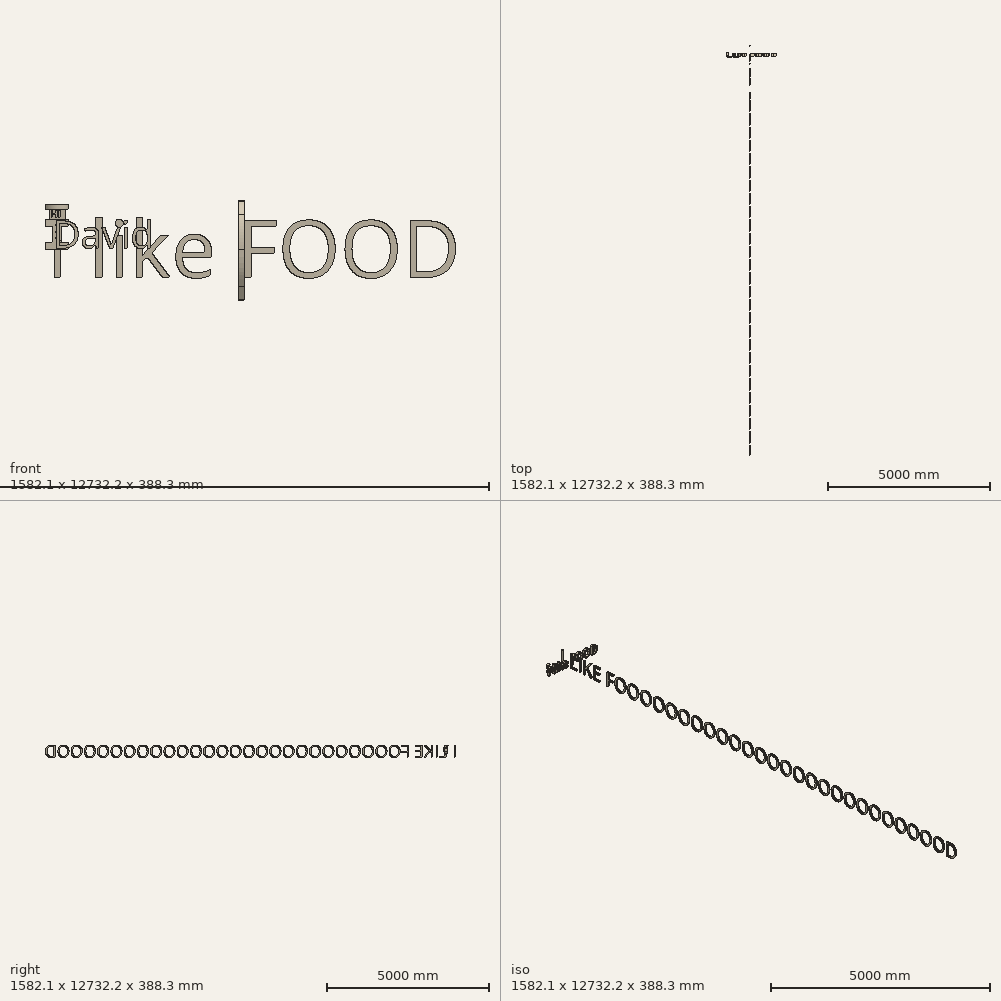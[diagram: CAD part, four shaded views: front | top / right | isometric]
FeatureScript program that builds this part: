
annotation { "Feature Type Name" : "Feature", "Feature Type Description" : "" }
export const myFeature = defineFeature(function(context is Context, id is Id, definition is map)
    precondition{}
    {
        {
            var Q0;
            Q0=qCreatedBy(makeId("Front.planeOp"),FACE);
            var sketch = newSketch(context, id + "F0", { "sketchPlane" : qUnion([Q0])});
            skLineSegment(sketch, "E0", {"start": v(-45.38, -52.7) * mm, "end": v(43.52, -52.7) * mm});
            skLineSegment(sketch, "E1", {"start": v(43.52, -52.7) * mm, "end": v(43.52, -27.3) * mm});
            skLineSegment(sketch, "E2", {"start": v(43.52, -27.3) * mm, "end": v(18.12, -27.3) * mm});
            skLineSegment(sketch, "E3", {"start": v(18.12, -27.3) * mm, "end": v(18.12, 36.2) * mm});
            skLineSegment(sketch, "E4", {"start": v(18.12, 36.2) * mm, "end": v(43.52, 36.2) * mm});
            skLineSegment(sketch, "E5", {"start": v(43.52, 36.2) * mm, "end": v(43.52, 61.6) * mm});
            skLineSegment(sketch, "E6", {"start": v(43.52, 61.6) * mm, "end": v(-45.38, 61.6) * mm});
            skLineSegment(sketch, "E7", {"start": v(-45.38, 61.6) * mm, "end": v(-45.38, 36.2) * mm});
            skLineSegment(sketch, "E8", {"start": v(-45.38, 36.2) * mm, "end": v(-19.98, 36.2) * mm});
            skLineSegment(sketch, "E9", {"start": v(-19.98, 36.2) * mm, "end": v(-19.98, -27.3) * mm});
            skLineSegment(sketch, "E10", {"start": v(-19.98, -27.3) * mm, "end": v(-45.38, -27.3) * mm});
            skLineSegment(sketch, "E11", {"start": v(-45.38, -27.3) * mm, "end": v(-45.38, -52.7) * mm});
            skSolve(sketch);
        }
        {
            var Q0;
            Q0=makeQuery(id+"F0.imprint","IMPRINT",FACE,{"disambiguationData":[TD([[makeQuery(id+"F0.imprint","IMPRINT",EDGE,{"derivedFrom":sQuery(id+"F0.wireOp",EDGE,"E0")}),1.0]])]});
            extrude(context, id + "F1", {"entities" : qUnion([Q0]), "depth" : 76.2 * mm});
        }
        {
            var Q0;
            Q0=makeQuery(id+"F1.opExtrude","SWEPT_FACE",FACE,{"disambiguationData":[OSD([sQuery(id+"F0.wireOp",EDGE,"E9")])]});
            var sketch = newSketch(context, id + "F2", { "sketchPlane" : qUnion([Q0])});
            skCircle(sketch, "E12", {"center": v(38.1, 4.44) * mm, "radius": 23.75 * mm});
            skPoint(sketch, "E12.centerSnap0", {"position": v(0, 4.44) * mm});
            skPoint(sketch, "E12.centerSnap1", {"position": v(38.1, -27.3) * mm});
            skSolve(sketch);
        }
        {
            var Q0;
            Q0=makeQuery(id+"F2.imprint","IMPRINT",FACE,{"disambiguationData":[TD([[makeQuery(id+"F2.imprint","IMPRINT",EDGE,{"derivedFrom":sQuery(id+"F2.wireOp",EDGE,"E12")}),1.0]])]});
            extrude(context, id + "F3", {"entities" : qUnion([Q0]), "operationType" : NewBodyOperationType.REMOVE, "endBound" : BoundingType.THROUGH_ALL, "oppositeDirection" : true, "depth" : 25.4 * mm});
        }
        {
            var Q0;
            Q0=makeQuery(id+"F1.opExtrude","SWEPT_FACE",FACE,{"disambiguationData":[OSD([sQuery(id+"F0.wireOp",EDGE,"E6")])]});
            var sketch = newSketch(context, id + "F4", { "sketchPlane" : qUnion([Q0])});
            skLineSegment(sketch, "E13.bottom", {"start": v(-31.22, -11.65) * mm, "end": v(30, -11.65) * mm});
            skLineSegment(sketch, "E13.top", {"start": v(-31.22, -21.9) * mm, "end": v(30, -21.9) * mm});
            skLineSegment(sketch, "E13.left", {"start": v(-31.22, -11.65) * mm, "end": v(-31.22, -21.9) * mm});
            skLineSegment(sketch, "E13.right", {"start": v(30, -11.65) * mm, "end": v(30, -21.9) * mm});
            skSolve(sketch);
        }
        {
            var Q0;
            Q0 = qSketchRegion(id + "F4", true);
            extrude(context, id + "F5", {"entities" : qUnion([Q0]), "operationType" : NewBodyOperationType.ADD, "depth" : 40.9 * mm});
        }
        {
            var Q0;
            Q0=makeQuery(id+"F5.opExtrude","CAP_FACE",FACE,{"disambiguationData":[OSD([sQuery(id+"F4.wireOp",EDGE,"E13.bottom"),sQuery(id+"F4.wireOp",EDGE,"E13.top"),sQuery(id+"F4.wireOp",EDGE,"E13.left"),sQuery(id+"F4.wireOp",EDGE,"E13.right")])],"isStart":false});
            var sketch = newSketch(context, id + "F6", { "sketchPlane" : qUnion([Q0])});
            skCircle(sketch, "E14", {"center": v(-0.61, -15.13) * mm, "radius": 43.24 * mm});
            skPoint(sketch, "E14.centerSnap0", {"position": v(-0.61, -21.9) * mm});
            skSolve(sketch);
        }
        {
            var Q0;
            Q0 = qSketchRegion(id + "F6", true);
            extrude(context, id + "F7", {"entities" : qUnion([Q0]), "operationType" : NewBodyOperationType.ADD, "depth" : 18.54 * mm});
        }
        {
            var Q0;
            Q0=makeQuery(id+"F5.opExtrude","SWEPT_FACE",FACE,{"disambiguationData":[OSD([sQuery(id+"F4.wireOp",EDGE,"E13.top")])]});
            var sketch = newSketch(context, id + "F8", { "sketchPlane" : qUnion([Q0])});
            skText(sketch, "E15", { "text": "HI", "fontName": "OpenSans-Bold.ttf"});
            const initialGuessF8  = {"E15": [-0.02772, 0.06828, 1, 0, 0.02865]};
            skSetInitialGuess(sketch, initialGuessF8);
            skSolve(sketch);
        }
        {
            var Q0;
            Q0 = qSketchRegion(id + "F8", true);
            extrude(context, id + "F9", {"entities" : qUnion([Q0]), "operationType" : NewBodyOperationType.ADD, "depth" : 25.4 * mm});
        }
        {
            var Q0;
            Q0=makeQuery(id+"F1.opExtrude","CAP_FACE",FACE,{"disambiguationData":[OSD([sQuery(id+"F0.wireOp",EDGE,"E0"),sQuery(id+"F0.wireOp",EDGE,"E1"),sQuery(id+"F0.wireOp",EDGE,"E2"),sQuery(id+"F0.wireOp",EDGE,"E3"),sQuery(id+"F0.wireOp",EDGE,"E4"),sQuery(id+"F0.wireOp",EDGE,"E5"),sQuery(id+"F0.wireOp",EDGE,"E6"),sQuery(id+"F0.wireOp",EDGE,"E7"),sQuery(id+"F0.wireOp",EDGE,"E8"),sQuery(id+"F0.wireOp",EDGE,"E9"),sQuery(id+"F0.wireOp",EDGE,"E10"),sQuery(id+"F0.wireOp",EDGE,"E11")])],"isStart":false});
            var sketch = newSketch(context, id + "F10", { "sketchPlane" : qUnion([Q0])});
            skText(sketch, "E16", { "text": "David", "fontName": "OpenSans-Regular.ttf"});
            const initialGuessF10  = {"E16": [-0.01716, -0.04824, 1, 0, 0.10575]};
            skSetInitialGuess(sketch, initialGuessF10);
            skSolve(sketch);
        }
        {
            var Q0;
            Q0 = qSketchRegion(id + "F10", true);
            extrude(context, id + "F11", {"entities" : qUnion([Q0]), "operationType" : NewBodyOperationType.ADD, "depth" : 50.8 * mm});
        }
        {
            var Q0;
            Q0=qCreatedBy(makeId("Front.planeOp"),FACE);
            var sketch = newSketch(context, id + "F12", { "sketchPlane" : qUnion([Q0])});
            skText(sketch, "E17", { "text": "I like FOOD", "fontName": "OpenSans-Regular.ttf"});
            const initialGuessF12  = {"E17": [-0.04277, -0.16234, 1, 0, 0.2216]};
            skSetInitialGuess(sketch, initialGuessF12);
            skSolve(sketch);
        }
        {
            var Q0;
            Q0 = qSketchRegion(id + "F12", true);
            extrude(context, id + "F13", {"entities" : qUnion([Q0]), "depth" : 76.2 * mm});
        }
        {
            var Q0;
            Q0=makeQuery(id+"F13.opExtrude","SWEPT_FACE",FACE,{"disambiguationData":[OSD([sQuery(id+"F12.wireOp",EDGE,"E17.sketch_text.stroke-55")])]});
            var sketch = newSketch(context, id + "F14", { "sketchPlane" : qUnion([Q0])});
            skText(sketch, "E18", { "text": "I LIKE FOOOOOOOOOOOOOOOOOOOOOOOOOOD", "fontName": "OpenSans-Regular.ttf"});
            const initialGuessF14  = {"E18": [-0.3031, -0.24631, 1, 0, 0.38039]};
            skSetInitialGuess(sketch, initialGuessF14);
            skSolve(sketch);
        }
        {
            var Q0;
            Q0 = qSketchRegion(id + "F14", true);
            extrude(context, id + "F15", {"entities" : qUnion([Q0]), "operationType" : NewBodyOperationType.ADD, "depth" : 25.4 * mm});
        }
    });
